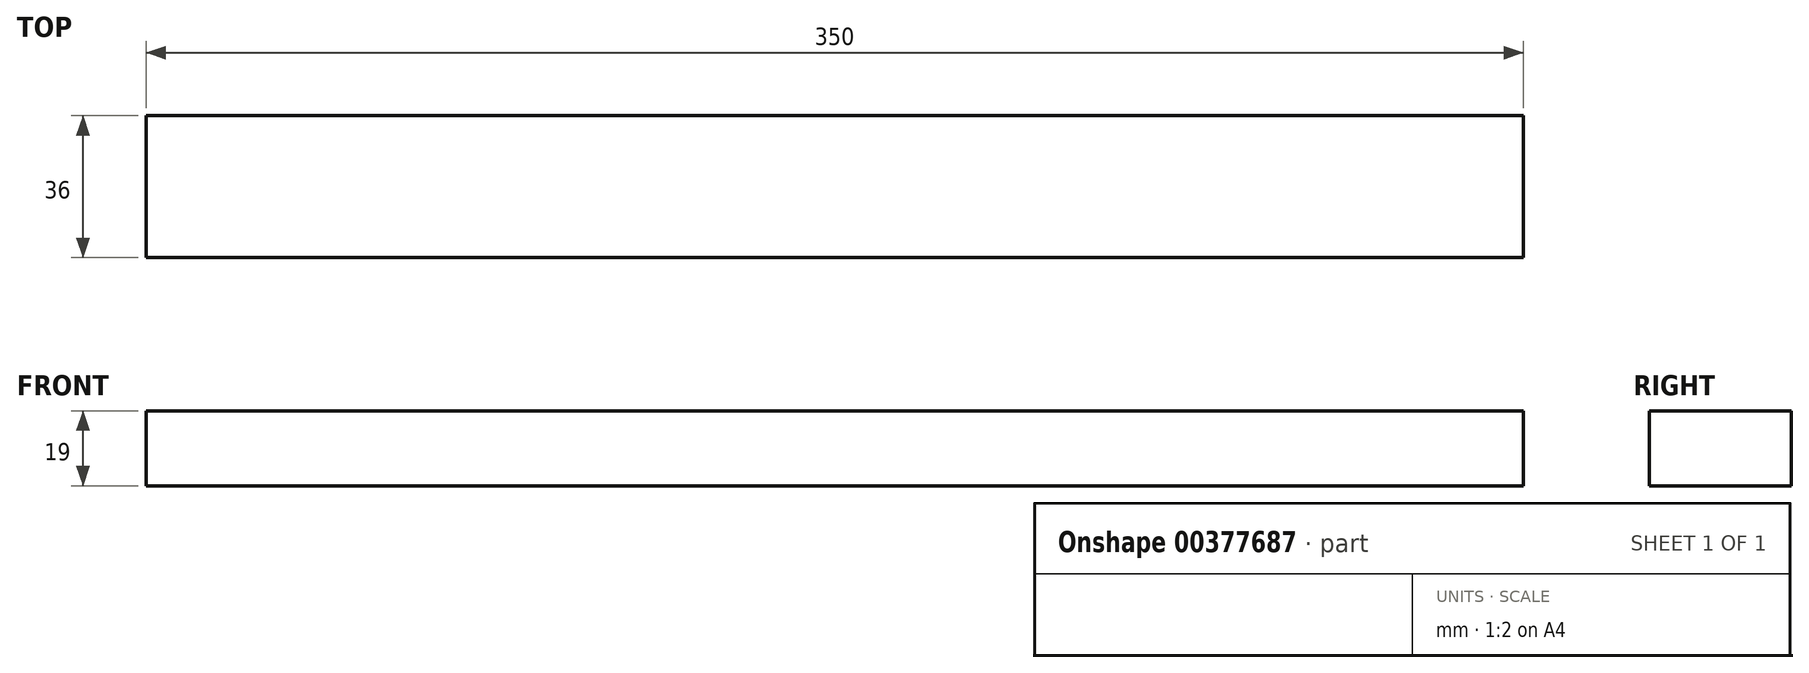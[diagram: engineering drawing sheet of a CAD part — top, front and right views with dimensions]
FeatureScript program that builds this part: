
annotation { "Feature Type Name" : "Feature", "Feature Type Description" : "" }
export const myFeature = defineFeature(function(context is Context, id is Id, definition is map)
    precondition{}
    {
        {
            var Q0;
            Q0=qCreatedBy(makeId("Top.planeOp"),FACE);
            var sketch = newSketch(context, id + "F0", { "sketchPlane" : qUnion([Q0])});
            skLineSegment(sketch, "E0.bottom", {"start": v(0, 0) * mm, "end": v(350, 0) * mm});
            skLineSegment(sketch, "E0.top", {"start": v(0, 36) * mm, "end": v(350, 36) * mm});
            skLineSegment(sketch, "E0.left", {"start": v(0, 0) * mm, "end": v(0, 36) * mm});
            skLineSegment(sketch, "E0.right", {"start": v(350, 0) * mm, "end": v(350, 36) * mm});
            skSolve(sketch);
        }
        {
            var Q0;
            Q0=makeQuery(id+"F0.imprint","IMPRINT",FACE,{"disambiguationData":[TD([[makeQuery(id+"F0.imprint","IMPRINT",EDGE,{"derivedFrom":sQuery(id+"F0.wireOp",EDGE,"E0.bottom")}),1.0]])]});
            extrude(context, id + "F1", {"entities" : qUnion([Q0]), "depth" : 19 * mm});
        }
    });
